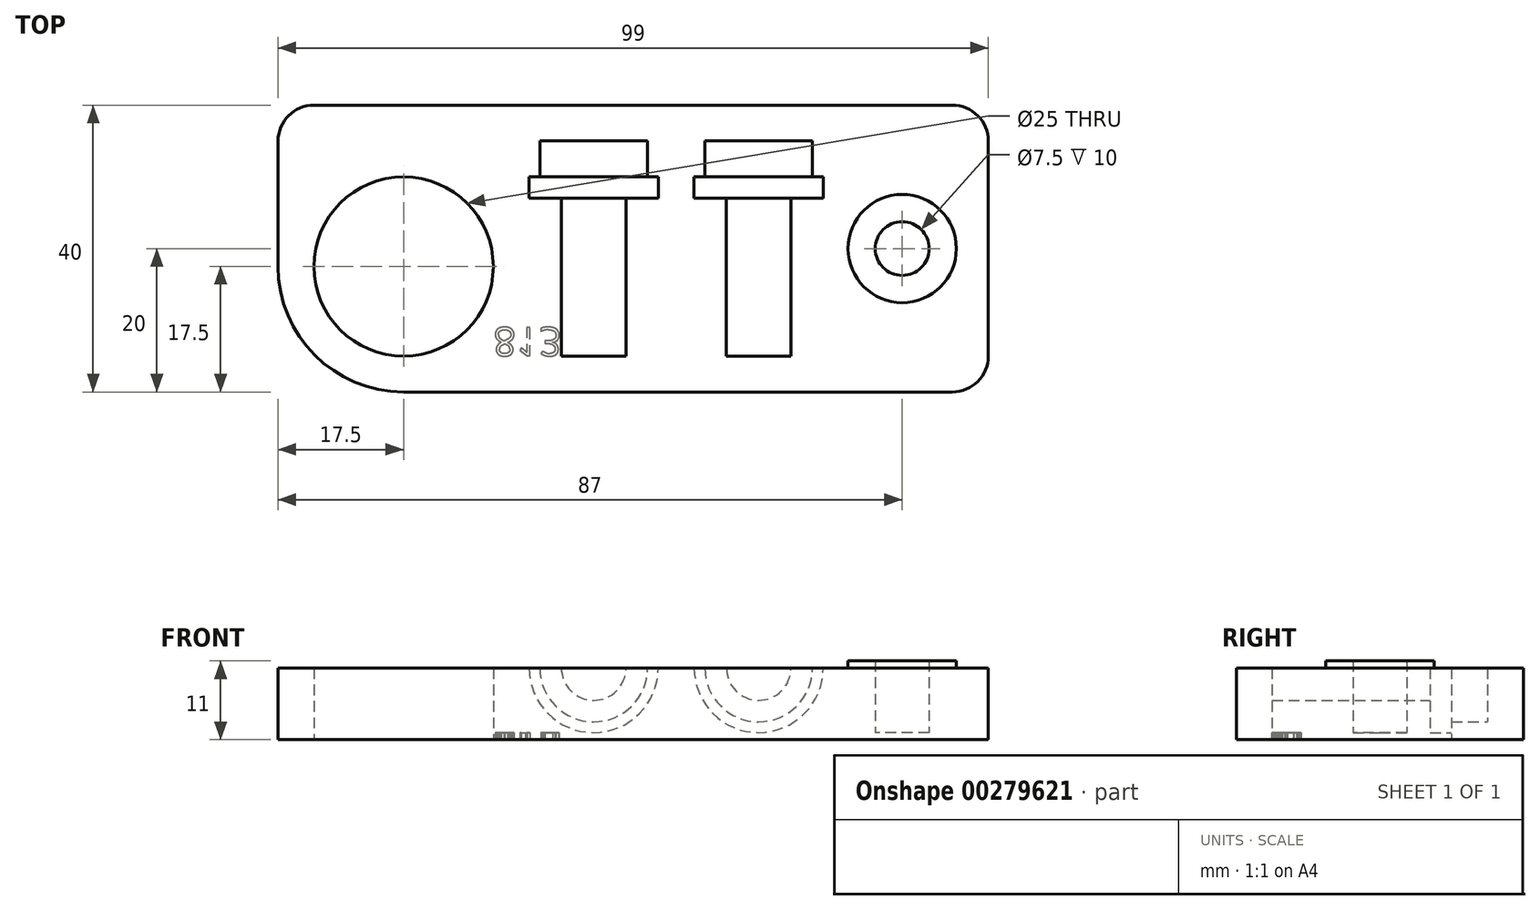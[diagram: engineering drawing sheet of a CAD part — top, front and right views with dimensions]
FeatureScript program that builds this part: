
annotation { "Feature Type Name" : "Feature", "Feature Type Description" : "" }
export const myFeature = defineFeature(function(context is Context, id is Id, definition is map)
    precondition{}
    {
        {
            var Q0;
            Q0=qCreatedBy(makeId("Top.planeOp"),FACE);
            var sketch = newSketch(context, id + "F0", { "sketchPlane" : qUnion([Q0])});
            skLineSegment(sketch, "E0.bottom", {"start": v(17.5, 0) * mm, "end": v(94, 0) * mm});
            skLineSegment(sketch, "E0.top", {"start": v(5, 40) * mm, "end": v(94, 40) * mm});
            skLineSegment(sketch, "E0.left", {"start": v(0, 17.5) * mm, "end": v(0, 35) * mm});
            skLineSegment(sketch, "E0.right", {"start": v(99, 5) * mm, "end": v(99, 35) * mm});
            skLineSegment(sketch, "E1.bottom", {"start": v(0, 0) * mm, "end": v(17.5, 0) * mm, "construction": true});
            skLineSegment(sketch, "E1.top", {"start": v(0, 17.5) * mm, "end": v(17.5, 17.5) * mm, "construction": true});
            skLineSegment(sketch, "E1.left", {"start": v(0, 0) * mm, "end": v(0, 17.5) * mm, "construction": true});
            skLineSegment(sketch, "E1.right", {"start": v(17.5, 0) * mm, "end": v(17.5, 17.5) * mm, "construction": true});
            skCircle(sketch, "E2", {"center": v(17.5, 17.5) * mm, "radius": 12.5 * mm});
            skPoint(sketch, "E3.visualSharp", {"position": v(0, 0) * mm});
            skArc(sketch, "E3.filletArc", {"start": v(0, 17.5) * mm, "mid": v(5.13, 5.13) * mm, "end": v(17.5, 0) * mm});
            skPoint(sketch, "E4.visualSharp", {"position": v(0, 40) * mm});
            skArc(sketch, "E4.filletArc", {"start": v(5, 40) * mm, "mid": v(1.46, 38.54) * mm, "end": v(0, 35) * mm});
            skPoint(sketch, "E5.visualSharp", {"position": v(99, 40) * mm});
            skArc(sketch, "E5.filletArc", {"start": v(99, 35) * mm, "mid": v(97.54, 38.54) * mm, "end": v(94, 40) * mm});
            skPoint(sketch, "E6.visualSharp", {"position": v(99, 0) * mm});
            skArc(sketch, "E6.filletArc", {"start": v(94, 0) * mm, "mid": v(97.54, 1.46) * mm, "end": v(99, 5) * mm});
            skSolve(sketch);
        }
        {
            var Q0;
            Q0=makeQuery(id+"F0.imprint","IMPRINT",FACE,{"disambiguationData":[TD([[makeQuery(id+"F0.imprint","IMPRINT",EDGE,{"derivedFrom":sQuery(id+"F0.wireOp",EDGE,"E0.bottom")}),1.0]])]});
            extrude(context, id + "F1", {"entities" : qUnion([Q0]), "depth" : 10 * mm});
        }
        {
            var Q0;
            Q0=makeQuery(id+"F1.opExtrude","CAP_FACE",FACE,{"disambiguationData":[OSD([sQuery(id+"F0.wireOp",EDGE,"E0.bottom"),sQuery(id+"F0.wireOp",EDGE,"E0.top"),sQuery(id+"F0.wireOp",EDGE,"E0.right"),sQuery(id+"F0.wireOp",EDGE,"E2"),sQuery(id+"F0.wireOp",EDGE,"E3.filletArc"),sQuery(id+"F0.wireOp",EDGE,"E4.filletArc"),sQuery(id+"F0.wireOp",EDGE,"E5.filletArc"),sQuery(id+"F0.wireOp",EDGE,"E6.filletArc")])],"isStart":false});
            var sketch = newSketch(context, id + "F2", { "sketchPlane" : qUnion([Q0])});
            skLineSegment(sketch, "E7.bottom", {"start": v(0, 0) * mm, "end": v(44, 0) * mm, "construction": true});
            skLineSegment(sketch, "E7.top", {"start": v(0, 5) * mm, "end": v(44, 5) * mm, "construction": true});
            skLineSegment(sketch, "E7.left", {"start": v(0, 0) * mm, "end": v(0, 5) * mm, "construction": true});
            skLineSegment(sketch, "E7.right", {"start": v(44, 0) * mm, "end": v(44, 5) * mm, "construction": true});
            skLineSegment(sketch, "E8.bottom", {"start": v(44, 5) * mm, "end": v(48.5, 5) * mm});
            skLineSegment(sketch, "E8.left", {"start": v(44, 5) * mm, "end": v(44, 27) * mm});
            skLineSegment(sketch, "E8.right", {"start": v(48.5, 5) * mm, "end": v(48.5, 27) * mm});
            skLineSegment(sketch, "E9.bottom", {"start": v(48.5, 27) * mm, "end": v(53, 27) * mm});
            skLineSegment(sketch, "E9.top", {"start": v(51.5, 30) * mm, "end": v(53, 30) * mm});
            skLineSegment(sketch, "E9.left", {"start": v(44, 27) * mm, "end": v(44, 30) * mm});
            skLineSegment(sketch, "E9.right", {"start": v(53, 27) * mm, "end": v(53, 30) * mm});
            skLineSegment(sketch, "E10.top", {"start": v(44, 35) * mm, "end": v(51.5, 35) * mm});
            skLineSegment(sketch, "E10.left", {"start": v(44, 30) * mm, "end": v(44, 35) * mm});
            skLineSegment(sketch, "E10.right", {"start": v(51.5, 30) * mm, "end": v(51.5, 35) * mm});
            skLineSegment(sketch, "E11", {"start": v(44, 5) * mm, "end": v(67, 5) * mm, "construction": true});
            skLineSegment(sketch, "E12.bottom", {"start": v(67, 5) * mm, "end": v(87, 5) * mm, "construction": true});
            skLineSegment(sketch, "E12.right", {"start": v(87, 5) * mm, "end": v(87, 20) * mm, "construction": true});
            skCircle(sketch, "E13", {"center": v(87, 20) * mm, "radius": 7.55 * mm});
            skCircle(sketch, "E14", {"center": v(87, 20) * mm, "radius": 3.75 * mm});
            skLineSegment(sketch, "E15.bottom", {"start": v(67, 5) * mm, "end": v(71.5, 5) * mm});
            skLineSegment(sketch, "E15.left", {"start": v(67, 5) * mm, "end": v(67, 27) * mm});
            skLineSegment(sketch, "E15.right", {"start": v(71.5, 5) * mm, "end": v(71.5, 27) * mm});
            skLineSegment(sketch, "E16.bottom", {"start": v(71.5, 27) * mm, "end": v(76, 27) * mm});
            skLineSegment(sketch, "E16.top", {"start": v(74.5, 30) * mm, "end": v(76, 30) * mm});
            skLineSegment(sketch, "E16.left", {"start": v(67, 27) * mm, "end": v(67, 30) * mm});
            skLineSegment(sketch, "E16.right", {"start": v(76, 27) * mm, "end": v(76, 30) * mm});
            skLineSegment(sketch, "E17.top", {"start": v(67, 35) * mm, "end": v(74.5, 35) * mm});
            skLineSegment(sketch, "E17.left", {"start": v(67, 30) * mm, "end": v(67, 35) * mm});
            skLineSegment(sketch, "E17.right", {"start": v(74.5, 30) * mm, "end": v(74.5, 35) * mm});
            skSolve(sketch);
        }
        {
            var Q0;
            Q0=makeQuery(id+"F2.imprint","IMPRINT",FACE,{"disambiguationData":[TD([[makeQuery(id+"F2.imprint","IMPRINT",EDGE,{"derivedFrom":sQuery(id+"F2.wireOp",EDGE,"E8.bottom")}),1.0]])]});
            var Q1;
            Q1=sQuery(id+"F2.wireOp",EDGE,"E8.left");
            revolve(context, id + "F3", {"operationType" : NewBodyOperationType.REMOVE, "entities" : qUnion([Q0]), "axis" : qUnion([Q1]), "revolveType" : RevolveType.FULL, "oppositeDirection" : true});
        }
        {
            var Q0;
            Q0=makeQuery(id+"F2.imprint","IMPRINT",FACE,{"disambiguationData":[TD([[makeQuery(id+"F2.imprint","IMPRINT",EDGE,{"derivedFrom":sQuery(id+"F2.wireOp",EDGE,"E15.bottom")}),1.0]])]});
            var Q1;
            Q1=sQuery(id+"F2.wireOp",EDGE,"E15.left");
            revolve(context, id + "F4", {"operationType" : NewBodyOperationType.REMOVE, "entities" : qUnion([Q0]), "axis" : qUnion([Q1]), "revolveType" : RevolveType.FULL, "oppositeDirection" : true});
        }
        {
            var Q0;
            Q0=makeQuery(id+"F2.imprint","IMPRINT",FACE,{"disambiguationData":[TD([[makeQuery(id+"F2.imprint","IMPRINT",EDGE,{"derivedFrom":sQuery(id+"F2.wireOp",EDGE,"E13")}),1.0]])]});
            extrude(context, id + "F5", {"entities" : qUnion([Q0]), "operationType" : NewBodyOperationType.ADD, "depth" : 1 * mm});
        }
        {
            var Q0;
            Q0=makeQuery(id+"F2.imprint","IMPRINT",FACE,{"disambiguationData":[TD([[makeQuery(id+"F2.imprint","IMPRINT",EDGE,{"derivedFrom":sQuery(id+"F2.wireOp",EDGE,"E14")}),1.0]])]});
            extrude(context, id + "F6", {"entities" : qUnion([Q0]), "operationType" : NewBodyOperationType.REMOVE, "oppositeDirection" : true, "depth" : 9 * mm});
        }
        {
            var Q0;
            Q0=makeQuery(id+"F1.opExtrude","CAP_FACE",FACE,{"disambiguationData":[OSD([sQuery(id+"F0.wireOp",EDGE,"E0.bottom"),sQuery(id+"F0.wireOp",EDGE,"E0.top"),sQuery(id+"F0.wireOp",EDGE,"E0.left"),sQuery(id+"F0.wireOp",EDGE,"E0.right"),sQuery(id+"F0.wireOp",EDGE,"E2"),sQuery(id+"F0.wireOp",EDGE,"E3.filletArc"),sQuery(id+"F0.wireOp",EDGE,"E4.filletArc"),sQuery(id+"F0.wireOp",EDGE,"E5.filletArc"),sQuery(id+"F0.wireOp",EDGE,"E6.filletArc")])],"isStart":true});
            var sketch = newSketch(context, id + "F7", { "sketchPlane" : qUnion([Q0])});
            skLineSegment(sketch, "E18.bottom", {"start": v(0, 0) * mm, "end": v(30, 0) * mm, "construction": true});
            skLineSegment(sketch, "E18.top", {"start": v(0, -5) * mm, "end": v(30, -5) * mm, "construction": true});
            skLineSegment(sketch, "E18.left", {"start": v(0, 0) * mm, "end": v(0, -5) * mm, "construction": true});
            skLineSegment(sketch, "E18.right", {"start": v(30, 0) * mm, "end": v(30, -5) * mm, "construction": true});
            skText(sketch, "E19", { "text": "813", "fontName": "OpenSans-Regular.ttf"});
            const initialGuessF7  = {"E19": [0.03, -0.009, 1, 0, 0.004]};
            skSetInitialGuess(sketch, initialGuessF7);
            skSolve(sketch);
        }
        {
            var Q0;
            Q0 = qSketchRegion(id + "F7", true);
            extrude(context, id + "F8", {"entities" : qUnion([Q0]), "operationType" : NewBodyOperationType.REMOVE, "oppositeDirection" : true, "depth" : 1 * mm});
        }
    });
